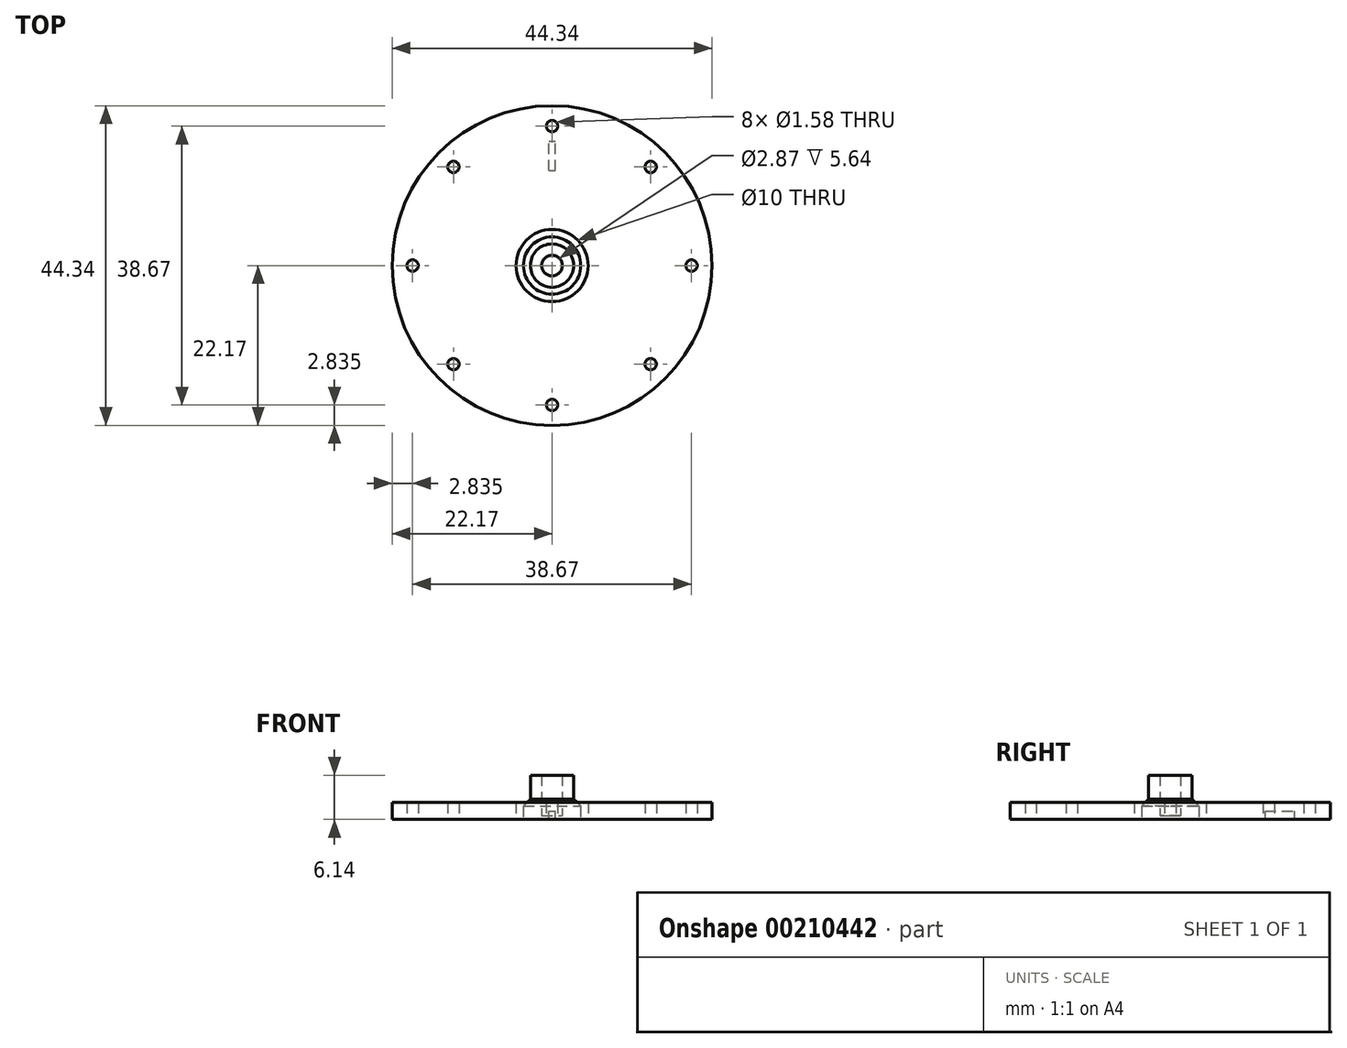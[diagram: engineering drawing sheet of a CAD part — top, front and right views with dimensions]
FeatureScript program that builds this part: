
annotation { "Feature Type Name" : "Feature", "Feature Type Description" : "" }
export const myFeature = defineFeature(function(context is Context, id is Id, definition is map)
    precondition{}
    {
        {
            var Q0;
            Q0=qCreatedBy(makeId("Top.planeOp"),FACE);
            var sketch = newSketch(context, id + "F0", { "sketchPlane" : qUnion([Q0])});
            skCircle(sketch, "E0", {"center": v(0, 0) * mm, "radius": 22.16 * mm});
            skCircle(sketch, "E1", {"center": v(0, 0) * mm, "radius": 5 * mm});
            skCircle(sketch, "E2", {"center": v(0, 0) * mm, "radius": 3.98 * mm});
            skCircle(sketch, "E3", {"center": v(0, 0) * mm, "radius": 3 * mm});
            skLineSegment(sketch, "E4", {"start": v(0, 0) * mm, "end": v(0, 19.34) * mm, "construction": true});
            skCircle(sketch, "E5", {"center": v(0, 19.34) * mm, "radius": 0.79 * mm});
            skCircle(sketch, "E6", {"center": v(0, 0) * mm, "radius": 1.44 * mm});
            skCircle(sketch, "E7.1.0", {"center": v(-13.67, 13.67) * mm, "radius": 0.79 * mm});
            skCircle(sketch, "E7.2.0", {"center": v(-19.34, 0) * mm, "radius": 0.79 * mm});
            skCircle(sketch, "E7.3.0", {"center": v(-13.67, -13.67) * mm, "radius": 0.79 * mm});
            skCircle(sketch, "E7.4.0", {"center": v(0, -19.34) * mm, "radius": 0.79 * mm});
            skCircle(sketch, "E7.5.0", {"center": v(13.67, -13.67) * mm, "radius": 0.79 * mm});
            skCircle(sketch, "E7.6.0", {"center": v(19.34, 0) * mm, "radius": 0.79 * mm});
            skCircle(sketch, "E7.7.0", {"center": v(13.67, 13.67) * mm, "radius": 0.79 * mm});
            skLineSegment(sketch, "E8.bottom", {"start": v(-0.43, 13.16) * mm, "end": v(0.43, 13.16) * mm});
            skLineSegment(sketch, "E8.top", {"start": v(-0.43, 17.27) * mm, "end": v(0.43, 17.27) * mm});
            skLineSegment(sketch, "E8.left", {"start": v(-0.43, 13.16) * mm, "end": v(-0.43, 17.27) * mm});
            skLineSegment(sketch, "E8.right", {"start": v(0.43, 13.16) * mm, "end": v(0.43, 17.27) * mm});
            skPoint(sketch, "E8.middle", {"position": v(0, 15.22) * mm});
            skSolve(sketch);
        }
        {
            var Q0;
            Q0=makeQuery(id+"F0.imprint","IMPRINT",FACE,{"disambiguationData":[TD([[makeQuery(id+"F0.imprint","IMPRINT",EDGE,{"derivedFrom":sQuery(id+"F0.wireOp",EDGE,"E0")}),1.0]])]});
            var Q1;
            Q1=makeQuery(id+"F0.imprint","IMPRINT",FACE,{"disambiguationData":[TD([[makeQuery(id+"F0.imprint","IMPRINT",EDGE,{"derivedFrom":sQuery(id+"F0.wireOp",EDGE,"E8.bottom")}),1.0]])]});
            extrude(context, id + "F1", {"entities" : qUnion([Q0, Q1]), "endBound" : BoundingType.SYMMETRIC, "depth" : 2.36 * mm});
        }
        {
            var Q0;
            Q0=makeQuery(id+"F1.opExtrude","CAP_FACE",FACE,{"disambiguationData":[OSD([sQuery(id+"F0.wireOp",EDGE,"E0"),sQuery(id+"F0.wireOp",EDGE,"E1"),sQuery(id+"F0.wireOp",EDGE,"E5"),sQuery(id+"F0.wireOp",EDGE,"E7.1.0"),sQuery(id+"F0.wireOp",EDGE,"E7.2.0"),sQuery(id+"F0.wireOp",EDGE,"E7.3.0"),sQuery(id+"F0.wireOp",EDGE,"E7.4.0"),sQuery(id+"F0.wireOp",EDGE,"E7.5.0"),sQuery(id+"F0.wireOp",EDGE,"E7.6.0"),sQuery(id+"F0.wireOp",EDGE,"E7.7.0")])],"isStart":true});
            var sketch = newSketch(context, id + "F2", { "sketchPlane" : qUnion([Q0])});
            skCircle(sketch, "E9.0", {"center": v(0, 0) * mm, "radius": 1.44 * mm});
            skCircle(sketch, "E9.1", {"center": v(0, 0) * mm, "radius": 3 * mm});
            skCircle(sketch, "E9.2", {"center": v(0, 0) * mm, "radius": 3.98 * mm});
            skCircle(sketch, "E9.3", {"center": v(0, 0) * mm, "radius": 5 * mm});
            skSolve(sketch);
        }
        {
            var Q0;
            Q0=makeQuery(id+"F2.imprint","IMPRINT",FACE,{"disambiguationData":[TD([[makeQuery(id+"F2.imprint","IMPRINT",EDGE,{"derivedFrom":sQuery(id+"F2.wireOp",EDGE,"E9.2")}),1.0]])]});
            extrude(context, id + "F3", {"entities" : qUnion([Q0]), "operationType" : NewBodyOperationType.ADD, "oppositeDirection" : true, "depth" : 2.86 * mm});
        }
        {
            var Q0;
            Q0=makeQuery(id+"F2.imprint","IMPRINT",FACE,{"disambiguationData":[TD([[makeQuery(id+"F2.imprint","IMPRINT",EDGE,{"derivedFrom":sQuery(id+"F2.wireOp",EDGE,"E9.1")}),1.0]])]});
            extrude(context, id + "F4", {"entities" : qUnion([Q0]), "operationType" : NewBodyOperationType.ADD, "oppositeDirection" : true, "depth" : 6.14 * mm});
        }
        {
            var Q0;
            Q0=makeQuery(id+"F2.imprint","IMPRINT",FACE,{"disambiguationData":[TD([[makeQuery(id+"F2.imprint","IMPRINT",EDGE,{"derivedFrom":sQuery(id+"F2.wireOp",EDGE,"E9.0")}),1.0]])]});
            extrude(context, id + "F5", {"entities" : qUnion([Q0]), "operationType" : NewBodyOperationType.ADD, "oppositeDirection" : true, "depth" : 0.5 * mm});
        }
        {
            var Q0;
            Q0=makeQuery(id+"F3.opExtrude","CAP_EDGE",EDGE,{"disambiguationData":[OSD([sQuery(id+"F2.wireOp",EDGE,"E9.2")])],"isStart":false});
            chamfer(context, id + "F6", {"entities" : qUnion([Q0]), "width" : 1 * mm, "tangentPropagation" : true});
        }
        {
            var Q0;
            Q0=makeQuery(id+"F0.imprint","IMPRINT",FACE,{"disambiguationData":[TD([[makeQuery(id+"F0.imprint","IMPRINT",EDGE,{"derivedFrom":sQuery(id+"F0.wireOp",EDGE,"E8.bottom")}),1.0]])]});
            extrude(context, id + "F7", {"entities" : qUnion([Q0]), "operationType" : NewBodyOperationType.REMOVE, "oppositeDirection" : true, "depth" : 25 * mm});
        }
    });
